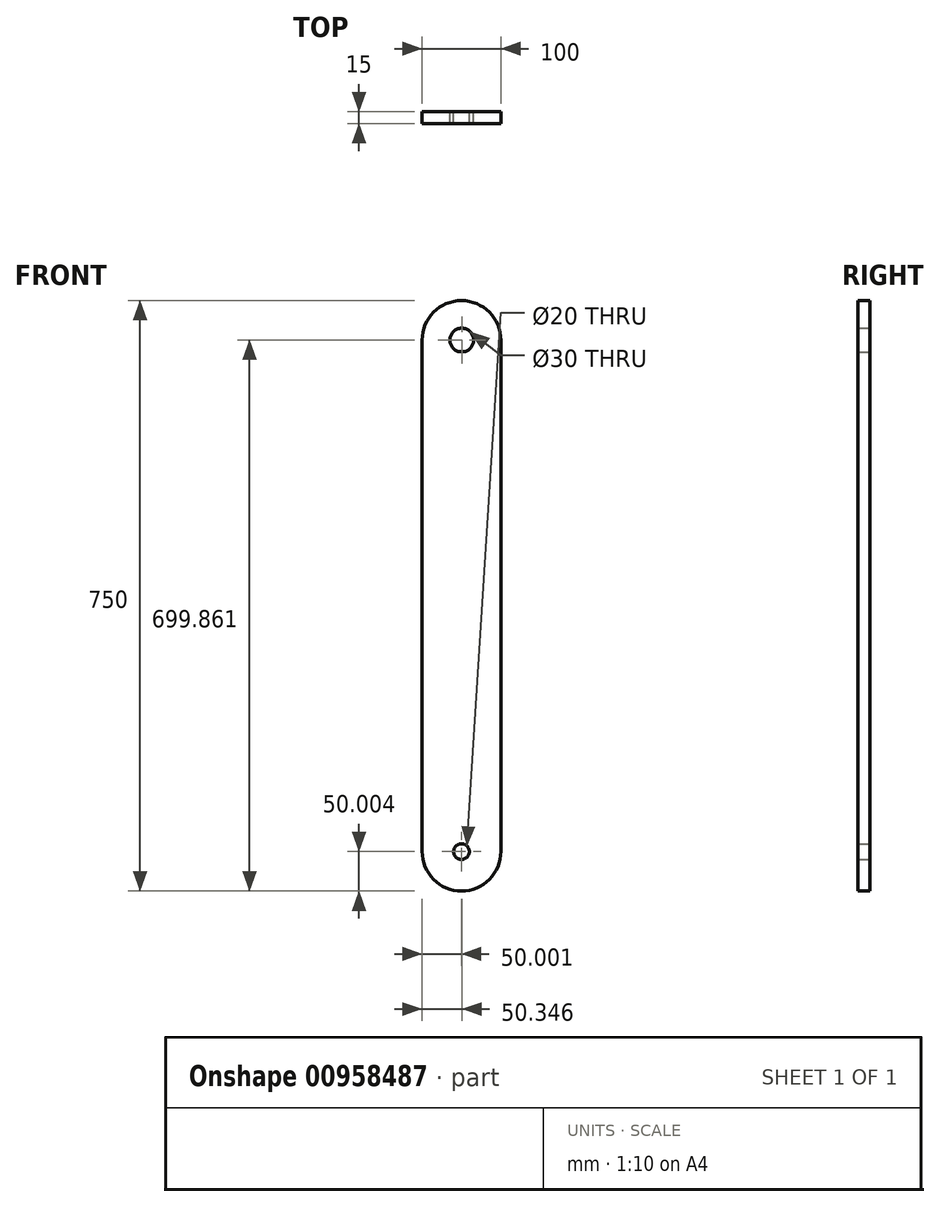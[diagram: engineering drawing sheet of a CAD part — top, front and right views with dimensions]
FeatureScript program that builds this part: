
annotation { "Feature Type Name" : "Feature", "Feature Type Description" : "" }
export const myFeature = defineFeature(function(context is Context, id is Id, definition is map)
    precondition{}
    {
        {
            var Q0;
            Q0=qCreatedBy(makeId("Front.planeOp"),FACE);
            var sketch = newSketch(context, id + "F0", { "sketchPlane" : qUnion([Q0])});
            skLineSegment(sketch, "E0.left", {"start": v(-7.16, 453.6) * mm, "end": v(-7.16, -196.4) * mm});
            skLineSegment(sketch, "E0.right", {"start": v(92.84, 453.6) * mm, "end": v(92.84, -196.4) * mm});
            skArc(sketch, "E1", {"start": v(92.84, 453.6) * mm, "mid": v(42.84, 503.6) * mm, "end": v(-7.16, 453.6) * mm});
            skArc(sketch, "E2", {"start": v(-7.16, -196.4) * mm, "mid": v(42.84, -246.4) * mm, "end": v(92.84, -196.4) * mm});
            skCircle(sketch, "E3", {"center": v(42.84, -196.4) * mm, "radius": 10 * mm});
            skCircle(sketch, "E4", {"center": v(43.19, 453.46) * mm, "radius": 15 * mm});
            skSolve(sketch);
        }
        {
            var Q0;
            Q0=makeQuery(id+"F0.imprint","IMPRINT",FACE,{"disambiguationData":[TD([[makeQuery(id+"F0.imprint","IMPRINT",EDGE,{"derivedFrom":sQuery(id+"F0.wireOp",EDGE,"E0.left")}),1.0]])]});
            extrude(context, id + "F1", {"entities" : qUnion([Q0]), "depth" : 15 * mm, "offsetDistance" : 25 * mm});
        }
    });
